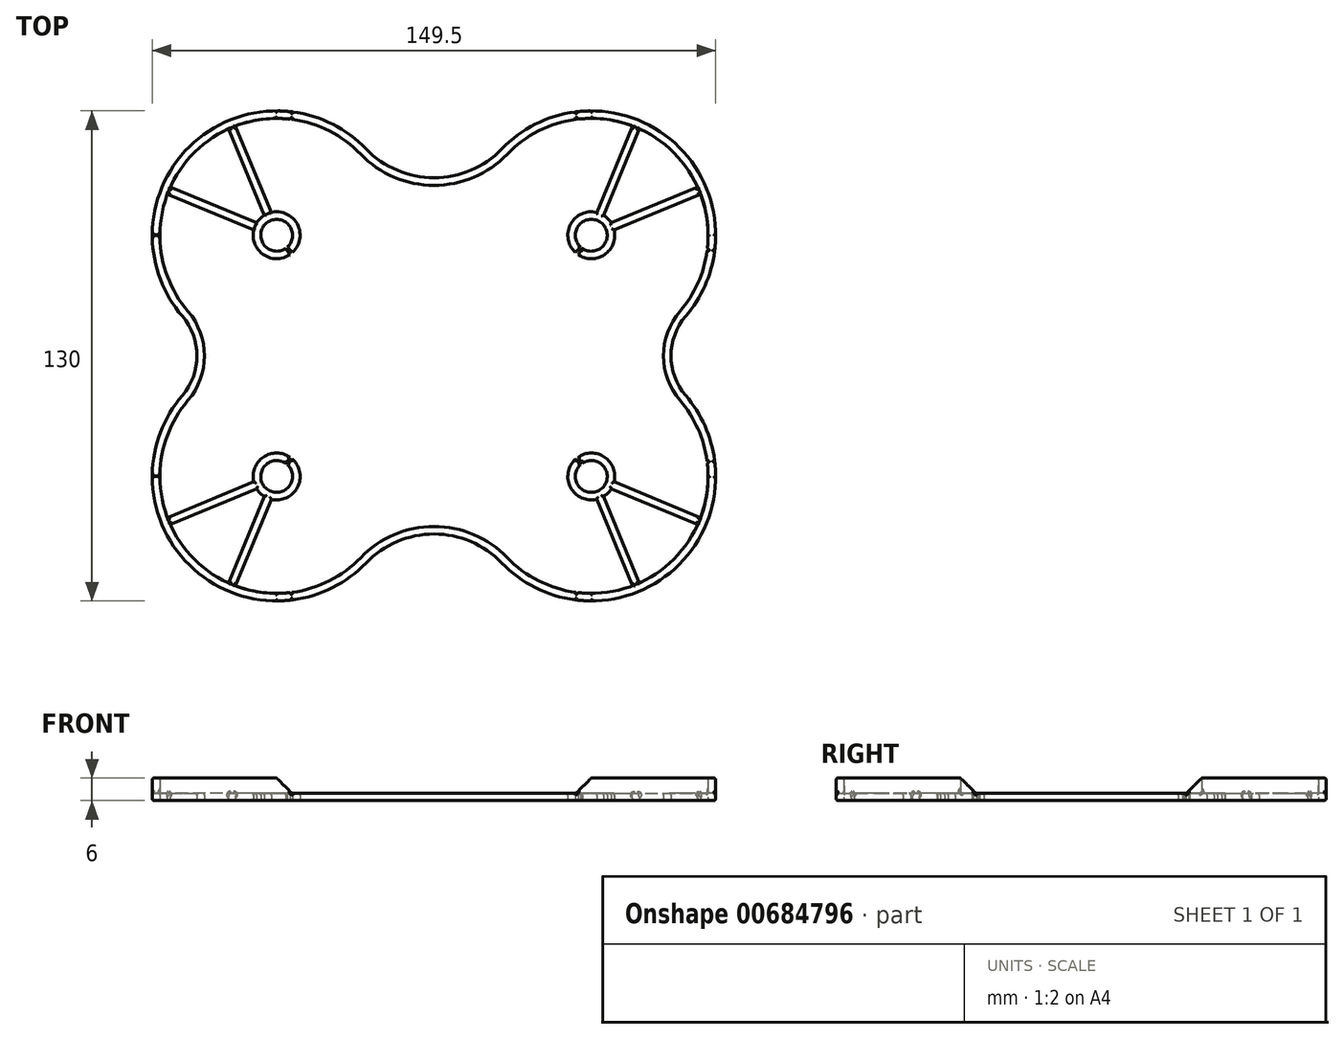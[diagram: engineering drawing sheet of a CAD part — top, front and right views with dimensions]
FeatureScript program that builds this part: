
annotation { "Feature Type Name" : "Feature", "Feature Type Description" : "" }
export const myFeature = defineFeature(function(context is Context, id is Id, definition is map)
    precondition{}
    {
        {
            var Q0;
            Q0=qCreatedBy(makeId("Top.planeOp"),FACE);
            var sketch = newSketch(context, id + "F0", { "sketchPlane" : qUnion([Q0])});
            skArc(sketch, "E0", {"start": v(2.86, -3.1) * mm, "mid": v(-2.63, 3.3) * mm, "end": v(2.4, -3.48) * mm});
            skArc(sketch, "E1.0", {"start": v(-3.28, 5.3) * mm, "mid": v(-4.4, 4.4) * mm, "end": v(-5.3, 3.28) * mm});
            skCircle(sketch, "E2", {"center": v(0, 0) * mm, "radius": 27 * mm, "construction": true});
            skArc(sketch, "E3.0", {"start": v(22.31, 21.52) * mm, "mid": v(6.81, 30.24) * mm, "end": v(-10.93, 29) * mm});
            skArc(sketch, "E4.0", {"start": v(23.75, 22.9) * mm, "mid": v(-22.2, 24.42) * mm, "end": v(-25.06, -21.47) * mm});
            skLineSegment(sketch, "E5", {"start": v(-58.95, -32) * mm, "end": v(56.7, -32) * mm, "construction": true});
            skArc(sketch, "E6.MirrorC", {"start": v(23.75, -86.9) * mm, "mid": v(-22.2, -88.42) * mm, "end": v(-25.06, -42.53) * mm});
            skArc(sketch, "E7.MirrorC", {"start": v(22.31, -85.52) * mm, "mid": v(6.81, -94.24) * mm, "end": v(-10.93, -93) * mm});
            skArc(sketch, "E8.MirrorC", {"start": v(-6.06, -65.43) * mm, "mid": v(-3.52, -58.86) * mm, "end": v(3.53, -58.87) * mm});
            skArc(sketch, "E9.MirrorC", {"start": v(2.86, -60.9) * mm, "mid": v(-2.63, -67.3) * mm, "end": v(2.4, -60.52) * mm});
            skArc(sketch, "E10", {"start": v(-25.06, -42.53) * mm, "mid": v(-21.17, -32) * mm, "end": v(-25.06, -21.47) * mm});
            skLineSegment(sketch, "E11", {"start": v(41.75, 0) * mm, "end": v(41.75, -120.97) * mm, "construction": true});
            skArc(sketch, "E12.MirrorC", {"start": v(80.64, -60.9) * mm, "mid": v(86.13, -67.3) * mm, "end": v(81.1, -60.52) * mm});
            skArc(sketch, "E13.MirrorC", {"start": v(86.78, -69.3) * mm, "mid": v(87.9, -68.4) * mm, "end": v(88.8, -67.28) * mm});
            skArc(sketch, "E14.MirrorC", {"start": v(80.64, -3.1) * mm, "mid": v(86.13, 3.3) * mm, "end": v(81.1, -3.48) * mm});
            skArc(sketch, "E15.MirrorC", {"start": v(86.78, 5.3) * mm, "mid": v(87.9, 4.4) * mm, "end": v(88.8, 3.28) * mm});
            skArc(sketch, "E16.MirrorCS", {"start": v(59.75, -86.9) * mm, "mid": v(105.7, -88.42) * mm, "end": v(108.56, -42.53) * mm});
            skArc(sketch, "E17.MirrorC", {"start": v(61.19, -85.52) * mm, "mid": v(76.69, -94.24) * mm, "end": v(94.43, -93) * mm});
            skArc(sketch, "E18.MirrorCS", {"start": v(108.56, -42.53) * mm, "mid": v(104.67, -32) * mm, "end": v(108.56, -21.47) * mm});
            skArc(sketch, "E19.MirrorCS", {"start": v(59.75, 22.9) * mm, "mid": v(105.7, 24.42) * mm, "end": v(108.56, -21.47) * mm});
            skArc(sketch, "E20.MirrorC", {"start": v(61.19, 21.52) * mm, "mid": v(76.69, 30.24) * mm, "end": v(94.43, 29) * mm});
            skArc(sketch, "E21", {"start": v(59.75, -86.9) * mm, "mid": v(41.75, -79.26) * mm, "end": v(23.75, -86.9) * mm});
            skArc(sketch, "E22.0", {"start": v(61.19, -85.52) * mm, "mid": v(41.75, -77.26) * mm, "end": v(22.31, -85.52) * mm});
            skArc(sketch, "E23.MirrorCS", {"start": v(61.19, 21.52) * mm, "mid": v(41.75, 13.26) * mm, "end": v(22.31, 21.52) * mm});
            skArc(sketch, "E24.MirrorCS", {"start": v(59.75, 22.9) * mm, "mid": v(41.75, 15.26) * mm, "end": v(23.75, 22.9) * mm});
            skArc(sketch, "E25.0", {"start": v(-23.54, -43.83) * mm, "mid": v(-19.17, -32) * mm, "end": v(-23.54, -20.17) * mm});
            skArc(sketch, "E26.0", {"start": v(107.04, -43.83) * mm, "mid": v(102.67, -32) * mm, "end": v(107.04, -20.17) * mm});
            skPoint(sketch, "E27.orphan", {"position": v(8.06, -32) * mm});
            skPoint(sketch, "E28.orphan", {"position": v(75.44, -32) * mm});
            skLineSegment(sketch, "E29", {"start": v(0, 0) * mm, "end": v(-28.64, 11.86) * mm, "construction": true});
            skLineSegment(sketch, "E30", {"start": v(0, 0) * mm, "end": v(-11.86, 28.64) * mm, "construction": true});
            skLineSegment(sketch, "E31.0", {"start": v(-6.06, 1.43) * mm, "end": v(-29.02, 10.94) * mm});
            skLineSegment(sketch, "E31.1", {"start": v(-1.43, 6.06) * mm, "end": v(-10.94, 29.02) * mm});
            skLineSegment(sketch, "E32.0", {"start": v(-5.3, 3.28) * mm, "end": v(-28.26, 12.79) * mm});
            skLineSegment(sketch, "E32.1", {"start": v(-3.28, 5.3) * mm, "end": v(-12.79, 28.26) * mm});
            skLineSegment(sketch, "E33.MirrorCS", {"start": v(-1.43, -70.06) * mm, "end": v(-10.94, -93.02) * mm});
            skLineSegment(sketch, "E34.MirrorCS", {"start": v(-3.28, -69.3) * mm, "end": v(-12.79, -92.26) * mm});
            skLineSegment(sketch, "E35.MirrorCS", {"start": v(-6.06, -65.43) * mm, "end": v(-29.02, -74.94) * mm});
            skLineSegment(sketch, "E36.MirrorCS", {"start": v(-5.3, -67.28) * mm, "end": v(-28.26, -76.79) * mm});
            skLineSegment(sketch, "E37.MirrorCS", {"start": v(84.93, 6.06) * mm, "end": v(94.44, 29.02) * mm});
            skLineSegment(sketch, "E38.MirrorCS", {"start": v(86.78, 5.3) * mm, "end": v(96.29, 28.26) * mm});
            skLineSegment(sketch, "E39.MirrorCS", {"start": v(88.8, 3.28) * mm, "end": v(111.76, 12.79) * mm});
            skLineSegment(sketch, "E40.MirrorCS", {"start": v(89.56, 1.43) * mm, "end": v(112.52, 10.94) * mm});
            skLineSegment(sketch, "E41.MirrorCS", {"start": v(89.56, -65.43) * mm, "end": v(112.52, -74.94) * mm});
            skLineSegment(sketch, "E42.MirrorCS", {"start": v(88.8, -67.28) * mm, "end": v(111.76, -76.79) * mm});
            skLineSegment(sketch, "E43.MirrorCS", {"start": v(86.78, -69.3) * mm, "end": v(96.29, -92.26) * mm});
            skLineSegment(sketch, "E44.MirrorCS", {"start": v(84.93, -70.06) * mm, "end": v(94.44, -93.02) * mm});
            skArc(sketch, "E45.trimOffspring", {"start": v(-6.06, 1.43) * mm, "mid": v(-3.52, -5.14) * mm, "end": v(3.53, -5.13) * mm});
            skArc(sketch, "E46.trimOffspring", {"start": v(-29, 10.93) * mm, "mid": v(-30.53, -5.36) * mm, "end": v(-23.54, -20.17) * mm});
            skArc(sketch, "E47.trimOffspring", {"start": v(-12.78, 28.24) * mm, "mid": v(-21.92, 21.92) * mm, "end": v(-28.24, 12.78) * mm});
            skArc(sketch, "E48.trimOffspring", {"start": v(-3.28, -69.3) * mm, "mid": v(-4.4, -68.4) * mm, "end": v(-5.3, -67.28) * mm});
            skArc(sketch, "E49.trimOffspring", {"start": v(-29, -74.93) * mm, "mid": v(-30.53, -58.64) * mm, "end": v(-23.54, -43.83) * mm});
            skArc(sketch, "E50.trimOffspring", {"start": v(-12.78, -92.24) * mm, "mid": v(-21.92, -85.92) * mm, "end": v(-28.24, -76.78) * mm});
            skArc(sketch, "E51.trimOffspring", {"start": v(89.56, -65.43) * mm, "mid": v(87.02, -58.86) * mm, "end": v(79.97, -58.87) * mm});
            skArc(sketch, "E52.trimOffspring", {"start": v(112.5, -74.93) * mm, "mid": v(114.03, -58.64) * mm, "end": v(107.04, -43.83) * mm});
            skArc(sketch, "E53.trimOffspring", {"start": v(96.28, -92.24) * mm, "mid": v(105.42, -85.92) * mm, "end": v(111.74, -76.78) * mm});
            skArc(sketch, "E54.trimOffspring", {"start": v(89.56, 1.43) * mm, "mid": v(87.02, -5.14) * mm, "end": v(79.97, -5.13) * mm});
            skArc(sketch, "E55.trimOffspring", {"start": v(96.28, 28.24) * mm, "mid": v(105.42, 21.92) * mm, "end": v(111.74, 12.78) * mm});
            skArc(sketch, "E56.trimOffspring", {"start": v(112.5, 10.93) * mm, "mid": v(114.03, -5.36) * mm, "end": v(107.04, -20.17) * mm});
            skLineSegment(sketch, "E57", {"start": v(2.4, -3.48) * mm, "end": v(3.53, -5.13) * mm});
            skLineSegment(sketch, "E58", {"start": v(2.86, -3.1) * mm, "end": v(4.22, -4.58) * mm});
            skArc(sketch, "E59.trimOffspring", {"start": v(4.22, -4.58) * mm, "mid": v(5.5, 2.92) * mm, "end": v(-1.43, 6.06) * mm});
            skLineSegment(sketch, "E60.MirrorCS", {"start": v(2.4, -60.52) * mm, "end": v(3.53, -58.87) * mm});
            skLineSegment(sketch, "E61.MirrorCS", {"start": v(2.86, -60.9) * mm, "end": v(4.22, -59.42) * mm});
            skLineSegment(sketch, "E62.MirrorCS", {"start": v(81.1, -3.48) * mm, "end": v(79.97, -5.13) * mm});
            skLineSegment(sketch, "E63.MirrorCS", {"start": v(80.64, -3.1) * mm, "end": v(79.28, -4.58) * mm});
            skLineSegment(sketch, "E64.MirrorCS", {"start": v(80.64, -60.9) * mm, "end": v(79.28, -59.42) * mm});
            skLineSegment(sketch, "E65.MirrorCS", {"start": v(81.1, -60.52) * mm, "end": v(79.97, -58.87) * mm});
            skArc(sketch, "E66.trimOffspring", {"start": v(4.22, -59.42) * mm, "mid": v(5.5, -66.92) * mm, "end": v(-1.43, -70.06) * mm});
            skArc(sketch, "E67.trimOffspring", {"start": v(79.28, -59.42) * mm, "mid": v(78, -66.92) * mm, "end": v(84.93, -70.06) * mm});
            skArc(sketch, "E68.trimOffspring", {"start": v(79.28, -4.58) * mm, "mid": v(78, 2.92) * mm, "end": v(84.93, 6.06) * mm});
            skSolve(sketch);
        }
        {
            var Q0;
            Q0=makeQuery(id+"F0.imprint","IMPRINT",FACE,{"disambiguationData":[TD([[makeQuery(id+"F0.imprint","IMPRINT",EDGE,{"derivedFrom":sQuery(id+"F0.wireOp",EDGE,"E0")}),-1.0]])]});
            extrude(context, id + "F1", {"entities" : qUnion([Q0]), "depth" : 2 * mm, "offsetDistance" : 25 * mm});
        }
        {
            var Q0;
            Q0=makeQuery(id+"F1.opExtrude","CAP_FACE",FACE,{"disambiguationData":[OSD([sQuery(id+"F0.wireOp",EDGE,"E0"),sQuery(id+"F0.wireOp",EDGE,"E1.0"),sQuery(id+"F0.wireOp",EDGE,"E3.0"),sQuery(id+"F0.wireOp",EDGE,"E4.0"),sQuery(id+"F0.wireOp",EDGE,"E6.MirrorC"),sQuery(id+"F0.wireOp",EDGE,"E7.MirrorC"),sQuery(id+"F0.wireOp",EDGE,"E8.MirrorC"),sQuery(id+"F0.wireOp",EDGE,"E9.MirrorC"),sQuery(id+"F0.wireOp",EDGE,"E10"),sQuery(id+"F0.wireOp",EDGE,"E12.MirrorC"),sQuery(id+"F0.wireOp",EDGE,"E13.MirrorC"),sQuery(id+"F0.wireOp",EDGE,"E14.MirrorC"),sQuery(id+"F0.wireOp",EDGE,"E15.MirrorC"),sQuery(id+"F0.wireOp",EDGE,"E16.MirrorCS"),sQuery(id+"F0.wireOp",EDGE,"E17.MirrorC"),sQuery(id+"F0.wireOp",EDGE,"E18.MirrorCS"),sQuery(id+"F0.wireOp",EDGE,"E19.MirrorCS"),sQuery(id+"F0.wireOp",EDGE,"E20.MirrorC"),sQuery(id+"F0.wireOp",EDGE,"E21"),sQuery(id+"F0.wireOp",EDGE,"E22.0"),sQuery(id+"F0.wireOp",EDGE,"E23.MirrorCS"),sQuery(id+"F0.wireOp",EDGE,"E24.MirrorCS"),sQuery(id+"F0.wireOp",EDGE,"E25.0"),sQuery(id+"F0.wireOp",EDGE,"E26.0"),sQuery(id+"F0.wireOp",EDGE,"E31.0"),sQuery(id+"F0.wireOp",EDGE,"E31.1"),sQuery(id+"F0.wireOp",EDGE,"E32.0"),sQuery(id+"F0.wireOp",EDGE,"E32.1"),sQuery(id+"F0.wireOp",EDGE,"E33.MirrorCS"),sQuery(id+"F0.wireOp",EDGE,"E34.MirrorCS"),sQuery(id+"F0.wireOp",EDGE,"E35.MirrorCS"),sQuery(id+"F0.wireOp",EDGE,"E36.MirrorCS"),sQuery(id+"F0.wireOp",EDGE,"E37.MirrorCS"),sQuery(id+"F0.wireOp",EDGE,"E38.MirrorCS"),sQuery(id+"F0.wireOp",EDGE,"E39.MirrorCS"),sQuery(id+"F0.wireOp",EDGE,"E40.MirrorCS"),sQuery(id+"F0.wireOp",EDGE,"E41.MirrorCS"),sQuery(id+"F0.wireOp",EDGE,"E42.MirrorCS"),sQuery(id+"F0.wireOp",EDGE,"E43.MirrorCS"),sQuery(id+"F0.wireOp",EDGE,"E44.MirrorCS"),sQuery(id+"F0.wireOp",EDGE,"E45.trimOffspring"),sQuery(id+"F0.wireOp",EDGE,"E46.trimOffspring"),sQuery(id+"F0.wireOp",EDGE,"E47.trimOffspring"),sQuery(id+"F0.wireOp",EDGE,"E48.trimOffspring"),sQuery(id+"F0.wireOp",EDGE,"E49.trimOffspring"),sQuery(id+"F0.wireOp",EDGE,"E50.trimOffspring"),sQuery(id+"F0.wireOp",EDGE,"E51.trimOffspring"),sQuery(id+"F0.wireOp",EDGE,"E52.trimOffspring"),sQuery(id+"F0.wireOp",EDGE,"E53.trimOffspring"),sQuery(id+"F0.wireOp",EDGE,"E54.trimOffspring"),sQuery(id+"F0.wireOp",EDGE,"E55.trimOffspring"),sQuery(id+"F0.wireOp",EDGE,"E56.trimOffspring")])],"isStart":false});
            var sketch = newSketch(context, id + "F2", { "sketchPlane" : qUnion([Q0])});
            skArc(sketch, "E69.0", {"start": v(0, 33) * mm, "mid": v(-23.33, 23.33) * mm, "end": v(-33, 0) * mm});
            skLineSegment(sketch, "E70", {"start": v(0, 31) * mm, "end": v(0, 33) * mm});
            skLineSegment(sketch, "E71", {"start": v(-31, 0) * mm, "end": v(-33, 0) * mm});
            skPoint(sketch, "E72.orphan", {"position": v(22.31, 21.52) * mm});
            skPoint(sketch, "E73.orphan", {"position": v(23.75, 22.9) * mm});
            skPoint(sketch, "E74.orphan", {"position": v(-23.54, -20.17) * mm});
            skPoint(sketch, "E75.orphan", {"position": v(-25.06, -21.47) * mm});
            skArc(sketch, "E76", {"start": v(0, 31) * mm, "mid": v(-21.92, 21.92) * mm, "end": v(-31, 0) * mm});
            skPoint(sketch, "E77.0.end.orphan", {"position": v(-10.93, 29) * mm});
            skPoint(sketch, "E78.0.end.orphan", {"position": v(-28.24, 12.78) * mm});
            skPoint(sketch, "E78.0.start.orphan", {"position": v(-12.78, 28.24) * mm});
            skPoint(sketch, "E79.0.start.orphan", {"position": v(-29, 10.93) * mm});
            skLineSegment(sketch, "E80.MirrorCS", {"start": v(0, -95) * mm, "end": v(0, -97) * mm});
            skLineSegment(sketch, "E81.MirrorCS", {"start": v(-31, -64) * mm, "end": v(-33, -64) * mm});
            skArc(sketch, "E82.MirrorCS", {"start": v(0, -95) * mm, "mid": v(-21.92, -85.92) * mm, "end": v(-31, -64) * mm});
            skPoint(sketch, "E83.MirrorP", {"position": v(-12.78, -92.24) * mm});
            skArc(sketch, "E84.MirrorCS", {"start": v(0, -97) * mm, "mid": v(-23.33, -87.33) * mm, "end": v(-33, -64) * mm});
            skPoint(sketch, "E85.MirrorP", {"position": v(-28.24, -76.78) * mm});
            skPoint(sketch, "E86.MirrorP", {"position": v(-10.93, -93) * mm});
            skPoint(sketch, "E87.MirrorP", {"position": v(-29, -74.93) * mm});
            skLineSegment(sketch, "E88.MirrorCS", {"start": v(83.5, 31) * mm, "end": v(83.5, 33) * mm});
            skLineSegment(sketch, "E89.MirrorCS", {"start": v(83.5, -95) * mm, "end": v(83.5, -97) * mm});
            skLineSegment(sketch, "E90.MirrorCS", {"start": v(114.5, -64) * mm, "end": v(116.5, -64) * mm});
            skLineSegment(sketch, "E91.MirrorCS", {"start": v(114.5, 0) * mm, "end": v(116.5, 0) * mm});
            skPoint(sketch, "E92.MirrorP", {"position": v(111.74, -76.78) * mm});
            skPoint(sketch, "E93.MirrorP", {"position": v(108.56, -21.47) * mm});
            skPoint(sketch, "E94.MirrorP", {"position": v(107.04, -20.17) * mm});
            skPoint(sketch, "E95.MirrorP", {"position": v(112.5, 10.93) * mm});
            skArc(sketch, "E96.MirrorCS", {"start": v(83.5, 33) * mm, "mid": v(106.83, 23.33) * mm, "end": v(116.5, 0) * mm});
            skPoint(sketch, "E97.MirrorP", {"position": v(112.5, -74.93) * mm});
            skPoint(sketch, "E98.MirrorP", {"position": v(94.43, 29) * mm});
            skPoint(sketch, "E99.MirrorP", {"position": v(96.28, 28.24) * mm});
            skArc(sketch, "E100.MirrorCS", {"start": v(83.5, -95) * mm, "mid": v(105.42, -85.92) * mm, "end": v(114.5, -64) * mm});
            skArc(sketch, "E101.MirrorCS", {"start": v(83.5, 31) * mm, "mid": v(105.42, 21.92) * mm, "end": v(114.5, 0) * mm});
            skPoint(sketch, "E102.MirrorP", {"position": v(94.43, -93) * mm});
            skPoint(sketch, "E103.MirrorP", {"position": v(96.28, -92.24) * mm});
            skArc(sketch, "E104.MirrorCS", {"start": v(83.5, -97) * mm, "mid": v(106.83, -87.33) * mm, "end": v(116.5, -64) * mm});
            skPoint(sketch, "E105.MirrorP", {"position": v(111.74, 12.78) * mm});
            skSolve(sketch);
        }
        {
            var Q0;
            Q0=makeQuery(id+"F2.imprint","IMPRINT",FACE,{"disambiguationData":[TD([[makeQuery(id+"F2.imprint","IMPRINT",EDGE,{"derivedFrom":sQuery(id+"F2.wireOp",EDGE,"E69.0")}),1.0]])]});
            var Q1;
            {var subQ5=sQuery(id+"F2.wireOp",EDGE,"E80.MirrorCS");Q1=makeQuery(id+"F2.imprint","IMPRINT",FACE,{"disambiguationData":[TD([[makeQuery(id+"F2.imprint","IMPRINT",EDGE,{"derivedFrom":subQ5}),-1.0]])]});}
            var Q2;
            {var subQ5=sQuery(id+"F2.wireOp",EDGE,"E89.MirrorCS");Q2=makeQuery(id+"F2.imprint","IMPRINT",FACE,{"disambiguationData":[TD([[makeQuery(id+"F2.imprint","IMPRINT",EDGE,{"derivedFrom":subQ5}),1.0]])]});}
            var Q3;
            {var subQ5=sQuery(id+"F2.wireOp",EDGE,"E88.MirrorCS");Q3=makeQuery(id+"F2.imprint","IMPRINT",FACE,{"disambiguationData":[TD([[makeQuery(id+"F2.imprint","IMPRINT",EDGE,{"derivedFrom":subQ5}),-1.0]])]});}
            extrude(context, id + "F3", {"entities" : qUnion([Q0, Q1, Q2, Q3]), "operationType" : NewBodyOperationType.ADD, "depth" : 4 * mm, "offsetDistance" : 25 * mm});
        }
        {
            var Q0;
            Q0=makeQuery(id+"F3.opExtrude","CAP_EDGE",EDGE,{"disambiguationData":[OSD([sQuery(id+"F2.wireOp",EDGE,"E71")])],"isStart":true});
            var Q1;
            Q1=makeQuery(id+"F3.opExtrude","CAP_EDGE",EDGE,{"disambiguationData":[OSD([sQuery(id+"F2.wireOp",EDGE,"E70")])],"isStart":true});
            var Q2;
            Q2=makeQuery(id+"F3.opExtrude","CAP_EDGE",EDGE,{"disambiguationData":[OSD([sQuery(id+"F2.wireOp",EDGE,"E88.MirrorCS")])],"isStart":true});
            var Q3;
            Q3=makeQuery(id+"F3.opExtrude","CAP_EDGE",EDGE,{"disambiguationData":[OSD([sQuery(id+"F2.wireOp",EDGE,"E91.MirrorCS")])],"isStart":true});
            var Q4;
            Q4=makeQuery(id+"F3.opExtrude","CAP_EDGE",EDGE,{"disambiguationData":[OSD([sQuery(id+"F2.wireOp",EDGE,"E90.MirrorCS")])],"isStart":true});
            var Q5;
            Q5=makeQuery(id+"F3.opExtrude","CAP_EDGE",EDGE,{"disambiguationData":[OSD([sQuery(id+"F2.wireOp",EDGE,"E89.MirrorCS")])],"isStart":true});
            var Q6;
            Q6=makeQuery(id+"F3.opExtrude","CAP_EDGE",EDGE,{"disambiguationData":[OSD([sQuery(id+"F2.wireOp",EDGE,"E80.MirrorCS")])],"isStart":true});
            var Q7;
            Q7=makeQuery(id+"F3.opExtrude","CAP_EDGE",EDGE,{"disambiguationData":[OSD([sQuery(id+"F2.wireOp",EDGE,"E81.MirrorCS")])],"isStart":true});
            chamfer(context, id + "F4", {"entities" : qUnion([Q0, Q1, Q2, Q3, Q4, Q5, Q6, Q7]), "width" : 4 * mm, "tangentPropagation" : true});
        }
        {
            var Q0;
            {var subQ0=sQuery(id+"F0.wireOp",EDGE,"E56.trimOffspring");var subQ1=sQuery(id+"F0.wireOp",EDGE,"E46.trimOffspring");var subQ2=sQuery(id+"F0.wireOp",EDGE,"E24.MirrorCS");var subQ3=sQuery(id+"F0.wireOp",EDGE,"E47.trimOffspring");var subQ4=sQuery(id+"F0.wireOp",EDGE,"E23.MirrorCS");var subQ5=sQuery(id+"F0.wireOp",EDGE,"E3.0");var subQ6=sQuery(id+"F0.wireOp",EDGE,"E55.trimOffspring");var subQ7=sQuery(id+"F0.wireOp",EDGE,"E20.MirrorC");var subQ8=sQuery(id+"F0.wireOp",EDGE,"E4.0");var subQ9=sQuery(id+"F0.wireOp",EDGE,"E19.MirrorCS");Q0=makeQuery(id+"F3.boolean.opBoolean","SPLIT",FACE,{"disambiguationData":[TD([makeQuery(id+"F1.opExtrude","SWEPT_FACE",FACE,{"disambiguationData":[OSD([subQ4])]})])],"derivedFrom":makeQuery(id+"F1.opExtrude","CAP_FACE",FACE,{"disambiguationData":[OSD([sQuery(id+"F0.wireOp",EDGE,"E0"),sQuery(id+"F0.wireOp",EDGE,"E1.0"),subQ5,subQ8,sQuery(id+"F0.wireOp",EDGE,"E6.MirrorC"),sQuery(id+"F0.wireOp",EDGE,"E7.MirrorC"),sQuery(id+"F0.wireOp",EDGE,"E8.MirrorC"),sQuery(id+"F0.wireOp",EDGE,"E9.MirrorC"),sQuery(id+"F0.wireOp",EDGE,"E10"),sQuery(id+"F0.wireOp",EDGE,"E12.MirrorC"),sQuery(id+"F0.wireOp",EDGE,"E13.MirrorC"),sQuery(id+"F0.wireOp",EDGE,"E14.MirrorC"),sQuery(id+"F0.wireOp",EDGE,"E15.MirrorC"),sQuery(id+"F0.wireOp",EDGE,"E16.MirrorCS"),sQuery(id+"F0.wireOp",EDGE,"E17.MirrorC"),sQuery(id+"F0.wireOp",EDGE,"E18.MirrorCS"),subQ9,subQ7,sQuery(id+"F0.wireOp",EDGE,"E21"),sQuery(id+"F0.wireOp",EDGE,"E22.0"),subQ4,subQ2,sQuery(id+"F0.wireOp",EDGE,"E25.0"),sQuery(id+"F0.wireOp",EDGE,"E26.0"),sQuery(id+"F0.wireOp",EDGE,"E31.0"),sQuery(id+"F0.wireOp",EDGE,"E31.1"),sQuery(id+"F0.wireOp",EDGE,"E32.0"),sQuery(id+"F0.wireOp",EDGE,"E32.1"),sQuery(id+"F0.wireOp",EDGE,"E33.MirrorCS"),sQuery(id+"F0.wireOp",EDGE,"E34.MirrorCS"),sQuery(id+"F0.wireOp",EDGE,"E35.MirrorCS"),sQuery(id+"F0.wireOp",EDGE,"E36.MirrorCS"),sQuery(id+"F0.wireOp",EDGE,"E37.MirrorCS"),sQuery(id+"F0.wireOp",EDGE,"E38.MirrorCS"),sQuery(id+"F0.wireOp",EDGE,"E39.MirrorCS"),sQuery(id+"F0.wireOp",EDGE,"E40.MirrorCS"),sQuery(id+"F0.wireOp",EDGE,"E41.MirrorCS"),sQuery(id+"F0.wireOp",EDGE,"E42.MirrorCS"),sQuery(id+"F0.wireOp",EDGE,"E43.MirrorCS"),sQuery(id+"F0.wireOp",EDGE,"E44.MirrorCS"),sQuery(id+"F0.wireOp",EDGE,"E45.trimOffspring"),subQ1,subQ3,sQuery(id+"F0.wireOp",EDGE,"E48.trimOffspring"),sQuery(id+"F0.wireOp",EDGE,"E49.trimOffspring"),sQuery(id+"F0.wireOp",EDGE,"E50.trimOffspring"),sQuery(id+"F0.wireOp",EDGE,"E51.trimOffspring"),sQuery(id+"F0.wireOp",EDGE,"E52.trimOffspring"),sQuery(id+"F0.wireOp",EDGE,"E53.trimOffspring"),sQuery(id+"F0.wireOp",EDGE,"E54.trimOffspring"),subQ6,subQ0])],"isStart":false})});}
            var Q1;
            {var subQ0=sQuery(id+"F0.wireOp",EDGE,"E46.trimOffspring");var subQ1=sQuery(id+"F0.wireOp",EDGE,"E45.trimOffspring");var subQ2=sQuery(id+"F0.wireOp",EDGE,"E32.1");var subQ3=sQuery(id+"F0.wireOp",EDGE,"E32.0");var subQ4=sQuery(id+"F0.wireOp",EDGE,"E31.1");var subQ5=sQuery(id+"F0.wireOp",EDGE,"E3.0");var subQ6=sQuery(id+"F0.wireOp",EDGE,"E47.trimOffspring");var subQ7=sQuery(id+"F0.wireOp",EDGE,"E0");var subQ8=sQuery(id+"F0.wireOp",EDGE,"E1.0");var subQ9=sQuery(id+"F0.wireOp",EDGE,"E31.0");Q1=makeQuery(id+"F3.boolean.opBoolean","SPLIT",FACE,{"disambiguationData":[TD([makeQuery(id+"F1.opExtrude","SWEPT_FACE",FACE,{"disambiguationData":[OSD([subQ7])]})])],"derivedFrom":makeQuery(id+"F1.opExtrude","CAP_FACE",FACE,{"disambiguationData":[OSD([subQ7,subQ8,subQ5,sQuery(id+"F0.wireOp",EDGE,"E4.0"),sQuery(id+"F0.wireOp",EDGE,"E6.MirrorC"),sQuery(id+"F0.wireOp",EDGE,"E7.MirrorC"),sQuery(id+"F0.wireOp",EDGE,"E8.MirrorC"),sQuery(id+"F0.wireOp",EDGE,"E9.MirrorC"),sQuery(id+"F0.wireOp",EDGE,"E10"),sQuery(id+"F0.wireOp",EDGE,"E12.MirrorC"),sQuery(id+"F0.wireOp",EDGE,"E13.MirrorC"),sQuery(id+"F0.wireOp",EDGE,"E14.MirrorC"),sQuery(id+"F0.wireOp",EDGE,"E15.MirrorC"),sQuery(id+"F0.wireOp",EDGE,"E16.MirrorCS"),sQuery(id+"F0.wireOp",EDGE,"E17.MirrorC"),sQuery(id+"F0.wireOp",EDGE,"E18.MirrorCS"),sQuery(id+"F0.wireOp",EDGE,"E19.MirrorCS"),sQuery(id+"F0.wireOp",EDGE,"E20.MirrorC"),sQuery(id+"F0.wireOp",EDGE,"E21"),sQuery(id+"F0.wireOp",EDGE,"E22.0"),sQuery(id+"F0.wireOp",EDGE,"E23.MirrorCS"),sQuery(id+"F0.wireOp",EDGE,"E24.MirrorCS"),sQuery(id+"F0.wireOp",EDGE,"E25.0"),sQuery(id+"F0.wireOp",EDGE,"E26.0"),subQ9,subQ4,subQ3,subQ2,sQuery(id+"F0.wireOp",EDGE,"E33.MirrorCS"),sQuery(id+"F0.wireOp",EDGE,"E34.MirrorCS"),sQuery(id+"F0.wireOp",EDGE,"E35.MirrorCS"),sQuery(id+"F0.wireOp",EDGE,"E36.MirrorCS"),sQuery(id+"F0.wireOp",EDGE,"E37.MirrorCS"),sQuery(id+"F0.wireOp",EDGE,"E38.MirrorCS"),sQuery(id+"F0.wireOp",EDGE,"E39.MirrorCS"),sQuery(id+"F0.wireOp",EDGE,"E40.MirrorCS"),sQuery(id+"F0.wireOp",EDGE,"E41.MirrorCS"),sQuery(id+"F0.wireOp",EDGE,"E42.MirrorCS"),sQuery(id+"F0.wireOp",EDGE,"E43.MirrorCS"),sQuery(id+"F0.wireOp",EDGE,"E44.MirrorCS"),subQ1,subQ0,subQ6,sQuery(id+"F0.wireOp",EDGE,"E48.trimOffspring"),sQuery(id+"F0.wireOp",EDGE,"E49.trimOffspring"),sQuery(id+"F0.wireOp",EDGE,"E50.trimOffspring"),sQuery(id+"F0.wireOp",EDGE,"E51.trimOffspring"),sQuery(id+"F0.wireOp",EDGE,"E52.trimOffspring"),sQuery(id+"F0.wireOp",EDGE,"E53.trimOffspring"),sQuery(id+"F0.wireOp",EDGE,"E54.trimOffspring"),sQuery(id+"F0.wireOp",EDGE,"E55.trimOffspring"),sQuery(id+"F0.wireOp",EDGE,"E56.trimOffspring")])],"isStart":false})});}
            var Q2;
            Q2=makeQuery(id+"F3.opExtrude","CAP_FACE",FACE,{"disambiguationData":[OSD([sQuery(id+"F2.wireOp",EDGE,"E69.0"),sQuery(id+"F2.wireOp",EDGE,"E70"),sQuery(id+"F2.wireOp",EDGE,"E71"),sQuery(id+"F2.wireOp",EDGE,"E76")])],"isStart":false});
            var Q3;
            {var subQ0=sQuery(id+"F0.wireOp",EDGE,"E50.trimOffspring");var subQ1=sQuery(id+"F0.wireOp",EDGE,"E25.0");var subQ2=sQuery(id+"F0.wireOp",EDGE,"E47.trimOffspring");var subQ3=sQuery(id+"F0.wireOp",EDGE,"E49.trimOffspring");var subQ4=sQuery(id+"F0.wireOp",EDGE,"E46.trimOffspring");var subQ5=sQuery(id+"F0.wireOp",EDGE,"E10");var subQ6=sQuery(id+"F0.wireOp",EDGE,"E3.0");var subQ7=sQuery(id+"F0.wireOp",EDGE,"E4.0");var subQ8=sQuery(id+"F0.wireOp",EDGE,"E6.MirrorC");var subQ9=sQuery(id+"F0.wireOp",EDGE,"E7.MirrorC");Q3=makeQuery(id+"F3.boolean.opBoolean","SPLIT",FACE,{"disambiguationData":[TD([makeQuery(id+"F1.opExtrude","SWEPT_FACE",FACE,{"disambiguationData":[OSD([subQ5])]})])],"derivedFrom":makeQuery(id+"F1.opExtrude","CAP_FACE",FACE,{"disambiguationData":[OSD([sQuery(id+"F0.wireOp",EDGE,"E0"),sQuery(id+"F0.wireOp",EDGE,"E1.0"),subQ6,subQ7,subQ8,subQ9,sQuery(id+"F0.wireOp",EDGE,"E8.MirrorC"),sQuery(id+"F0.wireOp",EDGE,"E9.MirrorC"),subQ5,sQuery(id+"F0.wireOp",EDGE,"E12.MirrorC"),sQuery(id+"F0.wireOp",EDGE,"E13.MirrorC"),sQuery(id+"F0.wireOp",EDGE,"E14.MirrorC"),sQuery(id+"F0.wireOp",EDGE,"E15.MirrorC"),sQuery(id+"F0.wireOp",EDGE,"E16.MirrorCS"),sQuery(id+"F0.wireOp",EDGE,"E17.MirrorC"),sQuery(id+"F0.wireOp",EDGE,"E18.MirrorCS"),sQuery(id+"F0.wireOp",EDGE,"E19.MirrorCS"),sQuery(id+"F0.wireOp",EDGE,"E20.MirrorC"),sQuery(id+"F0.wireOp",EDGE,"E21"),sQuery(id+"F0.wireOp",EDGE,"E22.0"),sQuery(id+"F0.wireOp",EDGE,"E23.MirrorCS"),sQuery(id+"F0.wireOp",EDGE,"E24.MirrorCS"),subQ1,sQuery(id+"F0.wireOp",EDGE,"E26.0"),sQuery(id+"F0.wireOp",EDGE,"E31.0"),sQuery(id+"F0.wireOp",EDGE,"E31.1"),sQuery(id+"F0.wireOp",EDGE,"E32.0"),sQuery(id+"F0.wireOp",EDGE,"E32.1"),sQuery(id+"F0.wireOp",EDGE,"E33.MirrorCS"),sQuery(id+"F0.wireOp",EDGE,"E34.MirrorCS"),sQuery(id+"F0.wireOp",EDGE,"E35.MirrorCS"),sQuery(id+"F0.wireOp",EDGE,"E36.MirrorCS"),sQuery(id+"F0.wireOp",EDGE,"E37.MirrorCS"),sQuery(id+"F0.wireOp",EDGE,"E38.MirrorCS"),sQuery(id+"F0.wireOp",EDGE,"E39.MirrorCS"),sQuery(id+"F0.wireOp",EDGE,"E40.MirrorCS"),sQuery(id+"F0.wireOp",EDGE,"E41.MirrorCS"),sQuery(id+"F0.wireOp",EDGE,"E42.MirrorCS"),sQuery(id+"F0.wireOp",EDGE,"E43.MirrorCS"),sQuery(id+"F0.wireOp",EDGE,"E44.MirrorCS"),sQuery(id+"F0.wireOp",EDGE,"E45.trimOffspring"),subQ4,subQ2,sQuery(id+"F0.wireOp",EDGE,"E48.trimOffspring"),subQ3,subQ0,sQuery(id+"F0.wireOp",EDGE,"E51.trimOffspring"),sQuery(id+"F0.wireOp",EDGE,"E52.trimOffspring"),sQuery(id+"F0.wireOp",EDGE,"E53.trimOffspring"),sQuery(id+"F0.wireOp",EDGE,"E54.trimOffspring"),sQuery(id+"F0.wireOp",EDGE,"E55.trimOffspring"),sQuery(id+"F0.wireOp",EDGE,"E56.trimOffspring")])],"isStart":false})});}
            var Q4;
            {var subQ0=sQuery(id+"F0.wireOp",EDGE,"E50.trimOffspring");var subQ1=sQuery(id+"F0.wireOp",EDGE,"E49.trimOffspring");var subQ2=sQuery(id+"F0.wireOp",EDGE,"E48.trimOffspring");var subQ3=sQuery(id+"F0.wireOp",EDGE,"E36.MirrorCS");var subQ4=sQuery(id+"F0.wireOp",EDGE,"E35.MirrorCS");var subQ5=sQuery(id+"F0.wireOp",EDGE,"E9.MirrorC");var subQ6=sQuery(id+"F0.wireOp",EDGE,"E7.MirrorC");var subQ7=sQuery(id+"F0.wireOp",EDGE,"E33.MirrorCS");var subQ8=sQuery(id+"F0.wireOp",EDGE,"E34.MirrorCS");var subQ9=sQuery(id+"F0.wireOp",EDGE,"E8.MirrorC");Q4=makeQuery(id+"F3.boolean.opBoolean","SPLIT",FACE,{"disambiguationData":[TD([makeQuery(id+"F1.opExtrude","SWEPT_FACE",FACE,{"disambiguationData":[OSD([subQ9])]})])],"derivedFrom":makeQuery(id+"F1.opExtrude","CAP_FACE",FACE,{"disambiguationData":[OSD([sQuery(id+"F0.wireOp",EDGE,"E0"),sQuery(id+"F0.wireOp",EDGE,"E1.0"),sQuery(id+"F0.wireOp",EDGE,"E3.0"),sQuery(id+"F0.wireOp",EDGE,"E4.0"),sQuery(id+"F0.wireOp",EDGE,"E6.MirrorC"),subQ6,subQ9,subQ5,sQuery(id+"F0.wireOp",EDGE,"E10"),sQuery(id+"F0.wireOp",EDGE,"E12.MirrorC"),sQuery(id+"F0.wireOp",EDGE,"E13.MirrorC"),sQuery(id+"F0.wireOp",EDGE,"E14.MirrorC"),sQuery(id+"F0.wireOp",EDGE,"E15.MirrorC"),sQuery(id+"F0.wireOp",EDGE,"E16.MirrorCS"),sQuery(id+"F0.wireOp",EDGE,"E17.MirrorC"),sQuery(id+"F0.wireOp",EDGE,"E18.MirrorCS"),sQuery(id+"F0.wireOp",EDGE,"E19.MirrorCS"),sQuery(id+"F0.wireOp",EDGE,"E20.MirrorC"),sQuery(id+"F0.wireOp",EDGE,"E21"),sQuery(id+"F0.wireOp",EDGE,"E22.0"),sQuery(id+"F0.wireOp",EDGE,"E23.MirrorCS"),sQuery(id+"F0.wireOp",EDGE,"E24.MirrorCS"),sQuery(id+"F0.wireOp",EDGE,"E25.0"),sQuery(id+"F0.wireOp",EDGE,"E26.0"),sQuery(id+"F0.wireOp",EDGE,"E31.0"),sQuery(id+"F0.wireOp",EDGE,"E31.1"),sQuery(id+"F0.wireOp",EDGE,"E32.0"),sQuery(id+"F0.wireOp",EDGE,"E32.1"),subQ7,subQ8,subQ4,subQ3,sQuery(id+"F0.wireOp",EDGE,"E37.MirrorCS"),sQuery(id+"F0.wireOp",EDGE,"E38.MirrorCS"),sQuery(id+"F0.wireOp",EDGE,"E39.MirrorCS"),sQuery(id+"F0.wireOp",EDGE,"E40.MirrorCS"),sQuery(id+"F0.wireOp",EDGE,"E41.MirrorCS"),sQuery(id+"F0.wireOp",EDGE,"E42.MirrorCS"),sQuery(id+"F0.wireOp",EDGE,"E43.MirrorCS"),sQuery(id+"F0.wireOp",EDGE,"E44.MirrorCS"),sQuery(id+"F0.wireOp",EDGE,"E45.trimOffspring"),sQuery(id+"F0.wireOp",EDGE,"E46.trimOffspring"),sQuery(id+"F0.wireOp",EDGE,"E47.trimOffspring"),subQ2,subQ1,subQ0,sQuery(id+"F0.wireOp",EDGE,"E51.trimOffspring"),sQuery(id+"F0.wireOp",EDGE,"E52.trimOffspring"),sQuery(id+"F0.wireOp",EDGE,"E53.trimOffspring"),sQuery(id+"F0.wireOp",EDGE,"E54.trimOffspring"),sQuery(id+"F0.wireOp",EDGE,"E55.trimOffspring"),sQuery(id+"F0.wireOp",EDGE,"E56.trimOffspring")])],"isStart":false})});}
            var Q5;
            Q5=makeQuery(id+"F3.opExtrude","CAP_FACE",FACE,{"disambiguationData":[OSD([sQuery(id+"F2.wireOp",EDGE,"E80.MirrorCS"),sQuery(id+"F2.wireOp",EDGE,"E81.MirrorCS"),sQuery(id+"F2.wireOp",EDGE,"E82.MirrorCS"),sQuery(id+"F2.wireOp",EDGE,"E84.MirrorCS")])],"isStart":false});
            var Q6;
            {var subQ0=sQuery(id+"F0.wireOp",EDGE,"E50.trimOffspring");var subQ1=sQuery(id+"F0.wireOp",EDGE,"E49.trimOffspring");var subQ2=sQuery(id+"F0.wireOp",EDGE,"E22.0");var subQ3=sQuery(id+"F0.wireOp",EDGE,"E21");var subQ4=sQuery(id+"F0.wireOp",EDGE,"E53.trimOffspring");var subQ5=sQuery(id+"F0.wireOp",EDGE,"E6.MirrorC");var subQ6=sQuery(id+"F0.wireOp",EDGE,"E52.trimOffspring");var subQ7=sQuery(id+"F0.wireOp",EDGE,"E17.MirrorC");var subQ8=sQuery(id+"F0.wireOp",EDGE,"E7.MirrorC");var subQ9=sQuery(id+"F0.wireOp",EDGE,"E16.MirrorCS");Q6=makeQuery(id+"F3.boolean.opBoolean","SPLIT",FACE,{"disambiguationData":[TD([makeQuery(id+"F1.opExtrude","SWEPT_FACE",FACE,{"disambiguationData":[OSD([subQ3])]})])],"derivedFrom":makeQuery(id+"F1.opExtrude","CAP_FACE",FACE,{"disambiguationData":[OSD([sQuery(id+"F0.wireOp",EDGE,"E0"),sQuery(id+"F0.wireOp",EDGE,"E1.0"),sQuery(id+"F0.wireOp",EDGE,"E3.0"),sQuery(id+"F0.wireOp",EDGE,"E4.0"),subQ5,subQ8,sQuery(id+"F0.wireOp",EDGE,"E8.MirrorC"),sQuery(id+"F0.wireOp",EDGE,"E9.MirrorC"),sQuery(id+"F0.wireOp",EDGE,"E10"),sQuery(id+"F0.wireOp",EDGE,"E12.MirrorC"),sQuery(id+"F0.wireOp",EDGE,"E13.MirrorC"),sQuery(id+"F0.wireOp",EDGE,"E14.MirrorC"),sQuery(id+"F0.wireOp",EDGE,"E15.MirrorC"),subQ9,subQ7,sQuery(id+"F0.wireOp",EDGE,"E18.MirrorCS"),sQuery(id+"F0.wireOp",EDGE,"E19.MirrorCS"),sQuery(id+"F0.wireOp",EDGE,"E20.MirrorC"),subQ3,subQ2,sQuery(id+"F0.wireOp",EDGE,"E23.MirrorCS"),sQuery(id+"F0.wireOp",EDGE,"E24.MirrorCS"),sQuery(id+"F0.wireOp",EDGE,"E25.0"),sQuery(id+"F0.wireOp",EDGE,"E26.0"),sQuery(id+"F0.wireOp",EDGE,"E31.0"),sQuery(id+"F0.wireOp",EDGE,"E31.1"),sQuery(id+"F0.wireOp",EDGE,"E32.0"),sQuery(id+"F0.wireOp",EDGE,"E32.1"),sQuery(id+"F0.wireOp",EDGE,"E33.MirrorCS"),sQuery(id+"F0.wireOp",EDGE,"E34.MirrorCS"),sQuery(id+"F0.wireOp",EDGE,"E35.MirrorCS"),sQuery(id+"F0.wireOp",EDGE,"E36.MirrorCS"),sQuery(id+"F0.wireOp",EDGE,"E37.MirrorCS"),sQuery(id+"F0.wireOp",EDGE,"E38.MirrorCS"),sQuery(id+"F0.wireOp",EDGE,"E39.MirrorCS"),sQuery(id+"F0.wireOp",EDGE,"E40.MirrorCS"),sQuery(id+"F0.wireOp",EDGE,"E41.MirrorCS"),sQuery(id+"F0.wireOp",EDGE,"E42.MirrorCS"),sQuery(id+"F0.wireOp",EDGE,"E43.MirrorCS"),sQuery(id+"F0.wireOp",EDGE,"E44.MirrorCS"),sQuery(id+"F0.wireOp",EDGE,"E45.trimOffspring"),sQuery(id+"F0.wireOp",EDGE,"E46.trimOffspring"),sQuery(id+"F0.wireOp",EDGE,"E47.trimOffspring"),sQuery(id+"F0.wireOp",EDGE,"E48.trimOffspring"),subQ1,subQ0,sQuery(id+"F0.wireOp",EDGE,"E51.trimOffspring"),subQ6,subQ4,sQuery(id+"F0.wireOp",EDGE,"E54.trimOffspring"),sQuery(id+"F0.wireOp",EDGE,"E55.trimOffspring"),sQuery(id+"F0.wireOp",EDGE,"E56.trimOffspring")])],"isStart":false})});}
            var Q7;
            Q7=makeQuery(id+"F3.opExtrude","CAP_FACE",FACE,{"disambiguationData":[OSD([sQuery(id+"F2.wireOp",EDGE,"E89.MirrorCS"),sQuery(id+"F2.wireOp",EDGE,"E90.MirrorCS"),sQuery(id+"F2.wireOp",EDGE,"E100.MirrorCS"),sQuery(id+"F2.wireOp",EDGE,"E104.MirrorCS")])],"isStart":false});
            var Q8;
            {var subQ0=sQuery(id+"F0.wireOp",EDGE,"E51.trimOffspring");var subQ1=sQuery(id+"F0.wireOp",EDGE,"E44.MirrorCS");var subQ2=sQuery(id+"F0.wireOp",EDGE,"E43.MirrorCS");var subQ3=sQuery(id+"F0.wireOp",EDGE,"E53.trimOffspring");var subQ4=sQuery(id+"F0.wireOp",EDGE,"E42.MirrorCS");var subQ5=sQuery(id+"F0.wireOp",EDGE,"E17.MirrorC");var subQ6=sQuery(id+"F0.wireOp",EDGE,"E12.MirrorC");var subQ7=sQuery(id+"F0.wireOp",EDGE,"E13.MirrorC");var subQ8=sQuery(id+"F0.wireOp",EDGE,"E52.trimOffspring");var subQ9=sQuery(id+"F0.wireOp",EDGE,"E41.MirrorCS");Q8=makeQuery(id+"F3.boolean.opBoolean","SPLIT",FACE,{"disambiguationData":[TD([makeQuery(id+"F1.opExtrude","SWEPT_FACE",FACE,{"disambiguationData":[OSD([subQ6])]})])],"derivedFrom":makeQuery(id+"F1.opExtrude","CAP_FACE",FACE,{"disambiguationData":[OSD([sQuery(id+"F0.wireOp",EDGE,"E0"),sQuery(id+"F0.wireOp",EDGE,"E1.0"),sQuery(id+"F0.wireOp",EDGE,"E3.0"),sQuery(id+"F0.wireOp",EDGE,"E4.0"),sQuery(id+"F0.wireOp",EDGE,"E6.MirrorC"),sQuery(id+"F0.wireOp",EDGE,"E7.MirrorC"),sQuery(id+"F0.wireOp",EDGE,"E8.MirrorC"),sQuery(id+"F0.wireOp",EDGE,"E9.MirrorC"),sQuery(id+"F0.wireOp",EDGE,"E10"),subQ6,subQ7,sQuery(id+"F0.wireOp",EDGE,"E14.MirrorC"),sQuery(id+"F0.wireOp",EDGE,"E15.MirrorC"),sQuery(id+"F0.wireOp",EDGE,"E16.MirrorCS"),subQ5,sQuery(id+"F0.wireOp",EDGE,"E18.MirrorCS"),sQuery(id+"F0.wireOp",EDGE,"E19.MirrorCS"),sQuery(id+"F0.wireOp",EDGE,"E20.MirrorC"),sQuery(id+"F0.wireOp",EDGE,"E21"),sQuery(id+"F0.wireOp",EDGE,"E22.0"),sQuery(id+"F0.wireOp",EDGE,"E23.MirrorCS"),sQuery(id+"F0.wireOp",EDGE,"E24.MirrorCS"),sQuery(id+"F0.wireOp",EDGE,"E25.0"),sQuery(id+"F0.wireOp",EDGE,"E26.0"),sQuery(id+"F0.wireOp",EDGE,"E31.0"),sQuery(id+"F0.wireOp",EDGE,"E31.1"),sQuery(id+"F0.wireOp",EDGE,"E32.0"),sQuery(id+"F0.wireOp",EDGE,"E32.1"),sQuery(id+"F0.wireOp",EDGE,"E33.MirrorCS"),sQuery(id+"F0.wireOp",EDGE,"E34.MirrorCS"),sQuery(id+"F0.wireOp",EDGE,"E35.MirrorCS"),sQuery(id+"F0.wireOp",EDGE,"E36.MirrorCS"),sQuery(id+"F0.wireOp",EDGE,"E37.MirrorCS"),sQuery(id+"F0.wireOp",EDGE,"E38.MirrorCS"),sQuery(id+"F0.wireOp",EDGE,"E39.MirrorCS"),sQuery(id+"F0.wireOp",EDGE,"E40.MirrorCS"),subQ9,subQ4,subQ2,subQ1,sQuery(id+"F0.wireOp",EDGE,"E45.trimOffspring"),sQuery(id+"F0.wireOp",EDGE,"E46.trimOffspring"),sQuery(id+"F0.wireOp",EDGE,"E47.trimOffspring"),sQuery(id+"F0.wireOp",EDGE,"E48.trimOffspring"),sQuery(id+"F0.wireOp",EDGE,"E49.trimOffspring"),sQuery(id+"F0.wireOp",EDGE,"E50.trimOffspring"),subQ0,subQ8,subQ3,sQuery(id+"F0.wireOp",EDGE,"E54.trimOffspring"),sQuery(id+"F0.wireOp",EDGE,"E55.trimOffspring"),sQuery(id+"F0.wireOp",EDGE,"E56.trimOffspring")])],"isStart":false})});}
            var Q9;
            {var subQ0=sQuery(id+"F0.wireOp",EDGE,"E56.trimOffspring");var subQ1=sQuery(id+"F0.wireOp",EDGE,"E26.0");var subQ2=sQuery(id+"F0.wireOp",EDGE,"E55.trimOffspring");var subQ3=sQuery(id+"F0.wireOp",EDGE,"E20.MirrorC");var subQ4=sQuery(id+"F0.wireOp",EDGE,"E16.MirrorCS");var subQ5=sQuery(id+"F0.wireOp",EDGE,"E52.trimOffspring");var subQ6=sQuery(id+"F0.wireOp",EDGE,"E17.MirrorC");var subQ7=sQuery(id+"F0.wireOp",EDGE,"E53.trimOffspring");var subQ8=sQuery(id+"F0.wireOp",EDGE,"E18.MirrorCS");var subQ9=sQuery(id+"F0.wireOp",EDGE,"E19.MirrorCS");Q9=makeQuery(id+"F3.boolean.opBoolean","SPLIT",FACE,{"disambiguationData":[TD([makeQuery(id+"F1.opExtrude","SWEPT_FACE",FACE,{"disambiguationData":[OSD([subQ8])]})])],"derivedFrom":makeQuery(id+"F1.opExtrude","CAP_FACE",FACE,{"disambiguationData":[OSD([sQuery(id+"F0.wireOp",EDGE,"E0"),sQuery(id+"F0.wireOp",EDGE,"E1.0"),sQuery(id+"F0.wireOp",EDGE,"E3.0"),sQuery(id+"F0.wireOp",EDGE,"E4.0"),sQuery(id+"F0.wireOp",EDGE,"E6.MirrorC"),sQuery(id+"F0.wireOp",EDGE,"E7.MirrorC"),sQuery(id+"F0.wireOp",EDGE,"E8.MirrorC"),sQuery(id+"F0.wireOp",EDGE,"E9.MirrorC"),sQuery(id+"F0.wireOp",EDGE,"E10"),sQuery(id+"F0.wireOp",EDGE,"E12.MirrorC"),sQuery(id+"F0.wireOp",EDGE,"E13.MirrorC"),sQuery(id+"F0.wireOp",EDGE,"E14.MirrorC"),sQuery(id+"F0.wireOp",EDGE,"E15.MirrorC"),subQ4,subQ6,subQ8,subQ9,subQ3,sQuery(id+"F0.wireOp",EDGE,"E21"),sQuery(id+"F0.wireOp",EDGE,"E22.0"),sQuery(id+"F0.wireOp",EDGE,"E23.MirrorCS"),sQuery(id+"F0.wireOp",EDGE,"E24.MirrorCS"),sQuery(id+"F0.wireOp",EDGE,"E25.0"),subQ1,sQuery(id+"F0.wireOp",EDGE,"E31.0"),sQuery(id+"F0.wireOp",EDGE,"E31.1"),sQuery(id+"F0.wireOp",EDGE,"E32.0"),sQuery(id+"F0.wireOp",EDGE,"E32.1"),sQuery(id+"F0.wireOp",EDGE,"E33.MirrorCS"),sQuery(id+"F0.wireOp",EDGE,"E34.MirrorCS"),sQuery(id+"F0.wireOp",EDGE,"E35.MirrorCS"),sQuery(id+"F0.wireOp",EDGE,"E36.MirrorCS"),sQuery(id+"F0.wireOp",EDGE,"E37.MirrorCS"),sQuery(id+"F0.wireOp",EDGE,"E38.MirrorCS"),sQuery(id+"F0.wireOp",EDGE,"E39.MirrorCS"),sQuery(id+"F0.wireOp",EDGE,"E40.MirrorCS"),sQuery(id+"F0.wireOp",EDGE,"E41.MirrorCS"),sQuery(id+"F0.wireOp",EDGE,"E42.MirrorCS"),sQuery(id+"F0.wireOp",EDGE,"E43.MirrorCS"),sQuery(id+"F0.wireOp",EDGE,"E44.MirrorCS"),sQuery(id+"F0.wireOp",EDGE,"E45.trimOffspring"),sQuery(id+"F0.wireOp",EDGE,"E46.trimOffspring"),sQuery(id+"F0.wireOp",EDGE,"E47.trimOffspring"),sQuery(id+"F0.wireOp",EDGE,"E48.trimOffspring"),sQuery(id+"F0.wireOp",EDGE,"E49.trimOffspring"),sQuery(id+"F0.wireOp",EDGE,"E50.trimOffspring"),sQuery(id+"F0.wireOp",EDGE,"E51.trimOffspring"),subQ5,subQ7,sQuery(id+"F0.wireOp",EDGE,"E54.trimOffspring"),subQ2,subQ0])],"isStart":false})});}
            var Q10;
            Q10=makeQuery(id+"F3.opExtrude","CAP_FACE",FACE,{"disambiguationData":[OSD([sQuery(id+"F2.wireOp",EDGE,"E88.MirrorCS"),sQuery(id+"F2.wireOp",EDGE,"E91.MirrorCS"),sQuery(id+"F2.wireOp",EDGE,"E96.MirrorCS"),sQuery(id+"F2.wireOp",EDGE,"E101.MirrorCS")])],"isStart":false});
            var Q11;
            {var subQ0=sQuery(id+"F0.wireOp",EDGE,"E56.trimOffspring");var subQ1=sQuery(id+"F0.wireOp",EDGE,"E54.trimOffspring");var subQ2=sQuery(id+"F0.wireOp",EDGE,"E40.MirrorCS");var subQ3=sQuery(id+"F0.wireOp",EDGE,"E15.MirrorC");var subQ4=sQuery(id+"F0.wireOp",EDGE,"E38.MirrorCS");var subQ5=sQuery(id+"F0.wireOp",EDGE,"E14.MirrorC");var subQ6=sQuery(id+"F0.wireOp",EDGE,"E39.MirrorCS");var subQ7=sQuery(id+"F0.wireOp",EDGE,"E55.trimOffspring");var subQ8=sQuery(id+"F0.wireOp",EDGE,"E20.MirrorC");var subQ9=sQuery(id+"F0.wireOp",EDGE,"E37.MirrorCS");Q11=makeQuery(id+"F3.boolean.opBoolean","SPLIT",FACE,{"disambiguationData":[TD([makeQuery(id+"F1.opExtrude","SWEPT_FACE",FACE,{"disambiguationData":[OSD([subQ5])]})])],"derivedFrom":makeQuery(id+"F1.opExtrude","CAP_FACE",FACE,{"disambiguationData":[OSD([sQuery(id+"F0.wireOp",EDGE,"E0"),sQuery(id+"F0.wireOp",EDGE,"E1.0"),sQuery(id+"F0.wireOp",EDGE,"E3.0"),sQuery(id+"F0.wireOp",EDGE,"E4.0"),sQuery(id+"F0.wireOp",EDGE,"E6.MirrorC"),sQuery(id+"F0.wireOp",EDGE,"E7.MirrorC"),sQuery(id+"F0.wireOp",EDGE,"E8.MirrorC"),sQuery(id+"F0.wireOp",EDGE,"E9.MirrorC"),sQuery(id+"F0.wireOp",EDGE,"E10"),sQuery(id+"F0.wireOp",EDGE,"E12.MirrorC"),sQuery(id+"F0.wireOp",EDGE,"E13.MirrorC"),subQ5,subQ3,sQuery(id+"F0.wireOp",EDGE,"E16.MirrorCS"),sQuery(id+"F0.wireOp",EDGE,"E17.MirrorC"),sQuery(id+"F0.wireOp",EDGE,"E18.MirrorCS"),sQuery(id+"F0.wireOp",EDGE,"E19.MirrorCS"),subQ8,sQuery(id+"F0.wireOp",EDGE,"E21"),sQuery(id+"F0.wireOp",EDGE,"E22.0"),sQuery(id+"F0.wireOp",EDGE,"E23.MirrorCS"),sQuery(id+"F0.wireOp",EDGE,"E24.MirrorCS"),sQuery(id+"F0.wireOp",EDGE,"E25.0"),sQuery(id+"F0.wireOp",EDGE,"E26.0"),sQuery(id+"F0.wireOp",EDGE,"E31.0"),sQuery(id+"F0.wireOp",EDGE,"E31.1"),sQuery(id+"F0.wireOp",EDGE,"E32.0"),sQuery(id+"F0.wireOp",EDGE,"E32.1"),sQuery(id+"F0.wireOp",EDGE,"E33.MirrorCS"),sQuery(id+"F0.wireOp",EDGE,"E34.MirrorCS"),sQuery(id+"F0.wireOp",EDGE,"E35.MirrorCS"),sQuery(id+"F0.wireOp",EDGE,"E36.MirrorCS"),subQ9,subQ4,subQ6,subQ2,sQuery(id+"F0.wireOp",EDGE,"E41.MirrorCS"),sQuery(id+"F0.wireOp",EDGE,"E42.MirrorCS"),sQuery(id+"F0.wireOp",EDGE,"E43.MirrorCS"),sQuery(id+"F0.wireOp",EDGE,"E44.MirrorCS"),sQuery(id+"F0.wireOp",EDGE,"E45.trimOffspring"),sQuery(id+"F0.wireOp",EDGE,"E46.trimOffspring"),sQuery(id+"F0.wireOp",EDGE,"E47.trimOffspring"),sQuery(id+"F0.wireOp",EDGE,"E48.trimOffspring"),sQuery(id+"F0.wireOp",EDGE,"E49.trimOffspring"),sQuery(id+"F0.wireOp",EDGE,"E50.trimOffspring"),sQuery(id+"F0.wireOp",EDGE,"E51.trimOffspring"),sQuery(id+"F0.wireOp",EDGE,"E52.trimOffspring"),sQuery(id+"F0.wireOp",EDGE,"E53.trimOffspring"),subQ1,subQ7,subQ0])],"isStart":false})});}
            var Q12;
            Q12=makeQuery(id+"F1.opExtrude","CAP_FACE",FACE,{"disambiguationData":[OSD([sQuery(id+"F0.wireOp",EDGE,"E0"),sQuery(id+"F0.wireOp",EDGE,"E1.0"),sQuery(id+"F0.wireOp",EDGE,"E3.0"),sQuery(id+"F0.wireOp",EDGE,"E4.0"),sQuery(id+"F0.wireOp",EDGE,"E6.MirrorC"),sQuery(id+"F0.wireOp",EDGE,"E7.MirrorC"),sQuery(id+"F0.wireOp",EDGE,"E8.MirrorC"),sQuery(id+"F0.wireOp",EDGE,"E9.MirrorC"),sQuery(id+"F0.wireOp",EDGE,"E10"),sQuery(id+"F0.wireOp",EDGE,"E12.MirrorC"),sQuery(id+"F0.wireOp",EDGE,"E13.MirrorC"),sQuery(id+"F0.wireOp",EDGE,"E14.MirrorC"),sQuery(id+"F0.wireOp",EDGE,"E15.MirrorC"),sQuery(id+"F0.wireOp",EDGE,"E16.MirrorCS"),sQuery(id+"F0.wireOp",EDGE,"E17.MirrorC"),sQuery(id+"F0.wireOp",EDGE,"E18.MirrorCS"),sQuery(id+"F0.wireOp",EDGE,"E19.MirrorCS"),sQuery(id+"F0.wireOp",EDGE,"E20.MirrorC"),sQuery(id+"F0.wireOp",EDGE,"E21"),sQuery(id+"F0.wireOp",EDGE,"E22.0"),sQuery(id+"F0.wireOp",EDGE,"E23.MirrorCS"),sQuery(id+"F0.wireOp",EDGE,"E24.MirrorCS"),sQuery(id+"F0.wireOp",EDGE,"E25.0"),sQuery(id+"F0.wireOp",EDGE,"E26.0"),sQuery(id+"F0.wireOp",EDGE,"E31.0"),sQuery(id+"F0.wireOp",EDGE,"E31.1"),sQuery(id+"F0.wireOp",EDGE,"E32.0"),sQuery(id+"F0.wireOp",EDGE,"E32.1"),sQuery(id+"F0.wireOp",EDGE,"E33.MirrorCS"),sQuery(id+"F0.wireOp",EDGE,"E34.MirrorCS"),sQuery(id+"F0.wireOp",EDGE,"E35.MirrorCS"),sQuery(id+"F0.wireOp",EDGE,"E36.MirrorCS"),sQuery(id+"F0.wireOp",EDGE,"E37.MirrorCS"),sQuery(id+"F0.wireOp",EDGE,"E38.MirrorCS"),sQuery(id+"F0.wireOp",EDGE,"E39.MirrorCS"),sQuery(id+"F0.wireOp",EDGE,"E40.MirrorCS"),sQuery(id+"F0.wireOp",EDGE,"E41.MirrorCS"),sQuery(id+"F0.wireOp",EDGE,"E42.MirrorCS"),sQuery(id+"F0.wireOp",EDGE,"E43.MirrorCS"),sQuery(id+"F0.wireOp",EDGE,"E44.MirrorCS"),sQuery(id+"F0.wireOp",EDGE,"E45.trimOffspring"),sQuery(id+"F0.wireOp",EDGE,"E46.trimOffspring"),sQuery(id+"F0.wireOp",EDGE,"E47.trimOffspring"),sQuery(id+"F0.wireOp",EDGE,"E48.trimOffspring"),sQuery(id+"F0.wireOp",EDGE,"E49.trimOffspring"),sQuery(id+"F0.wireOp",EDGE,"E50.trimOffspring"),sQuery(id+"F0.wireOp",EDGE,"E51.trimOffspring"),sQuery(id+"F0.wireOp",EDGE,"E52.trimOffspring"),sQuery(id+"F0.wireOp",EDGE,"E53.trimOffspring"),sQuery(id+"F0.wireOp",EDGE,"E54.trimOffspring"),sQuery(id+"F0.wireOp",EDGE,"E55.trimOffspring"),sQuery(id+"F0.wireOp",EDGE,"E56.trimOffspring")])],"isStart":true});
            fillet(context, id + "F5", {"entities" : qUnion([Q0, Q1, Q2, Q3, Q4, Q5, Q6, Q7, Q8, Q9, Q10, Q11, Q12]), "radius" : 0.5 * mm, "tangentPropagation" : true, "allowEdgeOverflow" : false});
        }
        {
            var Q0;
            Q0=qCreatedBy(makeId("Top.planeOp"),FACE);
            var sketch = newSketch(context, id + "F6", { "sketchPlane" : qUnion([Q0])});
            skArc(sketch, "E106.0", {"start": v(2.86, -3.1) * mm, "mid": v(-2.63, 3.3) * mm, "end": v(2.4, -3.48) * mm});
            skArc(sketch, "E107", {"start": v(4.22, -4.58) * mm, "mid": v(-3.88, 4.87) * mm, "end": v(3.53, -5.13) * mm});
            skLineSegment(sketch, "E108.0", {"start": v(2.86, -3.1) * mm, "end": v(4.22, -4.58) * mm});
            skLineSegment(sketch, "E109.0", {"start": v(2.4, -3.48) * mm, "end": v(3.53, -5.13) * mm});
            skPoint(sketch, "E110.0.end.orphan", {"position": v(-1.43, 6.06) * mm});
            skPoint(sketch, "E110.0.start.orphan", {"position": v(4.22, -4.58) * mm});
            skSolve(sketch);
        }
        {
            var Q0;
            Q0=makeQuery(id+"F6.imprint","IMPRINT",FACE,{"disambiguationData":[TD([[makeQuery(id+"F6.imprint","IMPRINT",EDGE,{"derivedFrom":sQuery(id+"F6.wireOp",EDGE,"E106.0")}),-1.0]])]});
            extrude(context, id + "F7", {"entities" : qUnion([Q0]), "depth" : 2 * mm, "offsetDistance" : 25 * mm});
        }
    });
